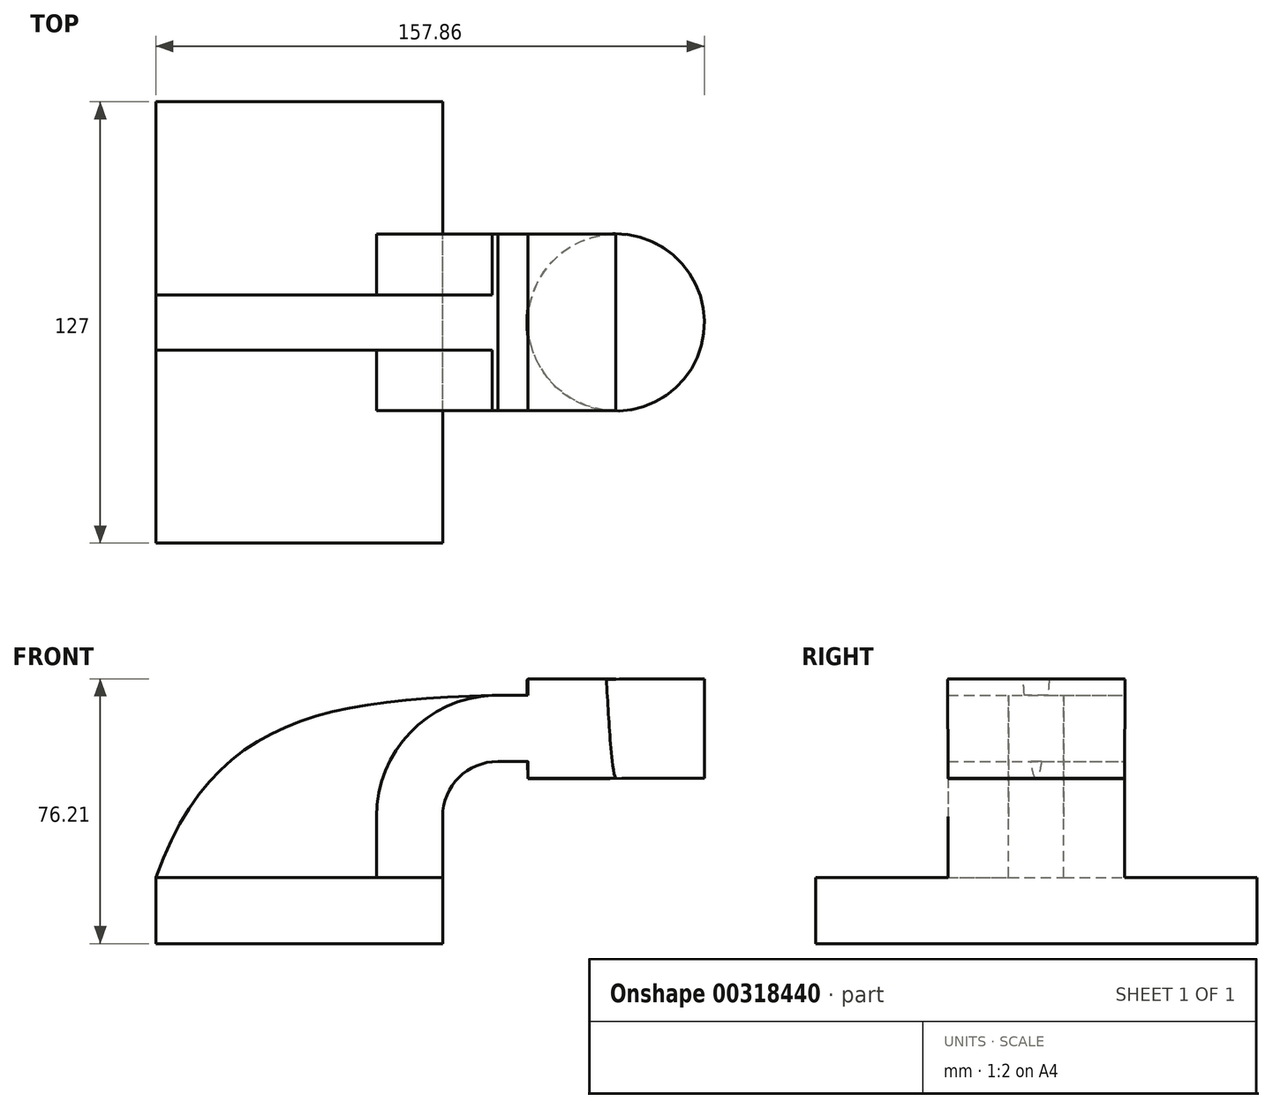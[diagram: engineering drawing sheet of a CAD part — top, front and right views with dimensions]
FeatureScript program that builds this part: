
annotation { "Feature Type Name" : "Feature", "Feature Type Description" : "" }
export const myFeature = defineFeature(function(context is Context, id is Id, definition is map)
    precondition{}
    {
        {
            var Q0;
            Q0=qCreatedBy(makeId("Front.planeOp"),FACE);
            var sketch = newSketch(context, id + "F0", { "sketchPlane" : qUnion([Q0])});
            skLineSegment(sketch, "E0.bottom", {"start": v(41.28, -9.52) * mm, "end": v(-41.28, -9.53) * mm});
            skLineSegment(sketch, "E0.top", {"start": v(41.28, 9.53) * mm, "end": v(-41.28, 9.53) * mm});
            skLineSegment(sketch, "E0.left", {"start": v(41.28, -9.52) * mm, "end": v(41.28, 9.53) * mm});
            skLineSegment(sketch, "E0.right", {"start": v(-41.28, -9.53) * mm, "end": v(-41.28, 9.53) * mm});
            skPoint(sketch, "E0.middle", {"position": v(0, 0) * mm});
            skLineSegment(sketch, "E1.bottom", {"start": v(65.78, 38.1) * mm, "end": v(116.58, 38.1) * mm});
            skLineSegment(sketch, "E1.top", {"start": v(65.78, 66.68) * mm, "end": v(116.58, 66.68) * mm});
            skLineSegment(sketch, "E1.left", {"start": v(65.78, 38.1) * mm, "end": v(65.78, 66.68) * mm});
            skLineSegment(sketch, "E1.right", {"start": v(116.58, 38.1) * mm, "end": v(116.58, 66.68) * mm});
            skPoint(sketch, "E1.middle", {"position": v(91.18, 52.39) * mm});
            skLineSegment(sketch, "E2", {"start": v(41.28, 9.53) * mm, "end": v(41.28, 27) * mm});
            skArc(sketch, "E3", {"start": v(41.27, 27) * mm, "mid": v(45.92, 38.23) * mm, "end": v(57.15, 42.88) * mm});
            skLineSegment(sketch, "E4", {"start": v(57.15, 42.88) * mm, "end": v(91.04, 42.88) * mm});
            skLineSegment(sketch, "E5.0", {"start": v(57.15, 61.93) * mm, "end": v(91.04, 61.93) * mm});
            skArc(sketch, "E5.1", {"start": v(22.23, 27) * mm, "mid": v(32.45, 51.7) * mm, "end": v(57.15, 61.93) * mm});
            skLineSegment(sketch, "E5.2", {"start": v(22.23, 9.53) * mm, "end": v(22.23, 27) * mm});
            skLineSegment(sketch, "E6", {"start": v(91.18, 38.1) * mm, "end": v(91.04, 66.68) * mm});
            skFitSpline(sketch, "E7", {"points": [v(-41.28, 9.53) * mm, v(57.15, 61.93) * mm], "startDerivative": vector(48.05, 133.54) * mm, "endDerivative": vector(156.47, 3.4) * mm});
            skSolve(sketch);
        }
        {
            var Q0;
            Q0=makeQuery(id+"F0.imprint","IMPRINT",FACE,{"disambiguationData":[TD([[makeQuery(id+"F0.imprint","IMPRINT",EDGE,{"derivedFrom":sQuery(id+"F0.wireOp",EDGE,"E0.bottom")}),-1.0]])]});
            extrude(context, id + "F1", {"entities" : qUnion([Q0]), "endBound" : BoundingType.SYMMETRIC, "depth" : 127 * mm});
        }
        {
            var Q0;
            {var subQ1=sQuery(id+"F0.wireOp",EDGE,"E2");Q0=makeQuery(id+"F0.imprint","IMPRINT",FACE,{"disambiguationData":[TD([[makeQuery(id+"F0.imprint","IMPRINT",EDGE,{"derivedFrom":subQ1}),1.0]])]});}
            extrude(context, id + "F2", {"entities" : qUnion([Q0]), "operationType" : NewBodyOperationType.ADD, "endBound" : BoundingType.SYMMETRIC, "depth" : 50.8 * mm});
        }
        {
            var Q0;
            {var subQ3=sQuery(id+"F0.wireOp",EDGE,"E5.2");Q0=makeQuery(id+"F0.imprint","IMPRINT",FACE,{"disambiguationData":[TD([[makeQuery(id+"F0.imprint","IMPRINT",EDGE,{"derivedFrom":subQ3}),1.0]])]});}
            extrude(context, id + "F3", {"entities" : qUnion([Q0]), "operationType" : NewBodyOperationType.ADD, "endBound" : BoundingType.SYMMETRIC, "depth" : 15.88 * mm});
        }
        {
            var Q0;
            {var subQ4=sQuery(id+"F0.wireOp",EDGE,"E6");Q0=makeQuery(id+"F0.imprint","IMPRINT",FACE,{"disambiguationData":[TD([[makeQuery(id+"F0.imprint","IMPRINT",EDGE,{"derivedFrom":subQ4}),1.0]])]});}
            extrude(context, id + "F4", {"entities" : qUnion([Q0]), "operationType" : NewBodyOperationType.ADD, "endBound" : BoundingType.SYMMETRIC, "depth" : 50.8 * mm});
        }
        {
            var Q0;
            {var subQ0=sQuery(id+"F0.wireOp",EDGE,"E1.right");Q0=makeQuery(id+"F0.imprint","IMPRINT",FACE,{"disambiguationData":[TD([[makeQuery(id+"F0.imprint","IMPRINT",EDGE,{"derivedFrom":subQ0}),1.0]])]});}
            var Q1;
            Q1=sQuery(id+"F0.wireOp",EDGE,"E6");
            revolve(context, id + "F5", {"operationType" : NewBodyOperationType.ADD, "entities" : qUnion([Q0]), "axis" : qUnion([Q1]), "revolveType" : RevolveType.FULL});
        }
    });
